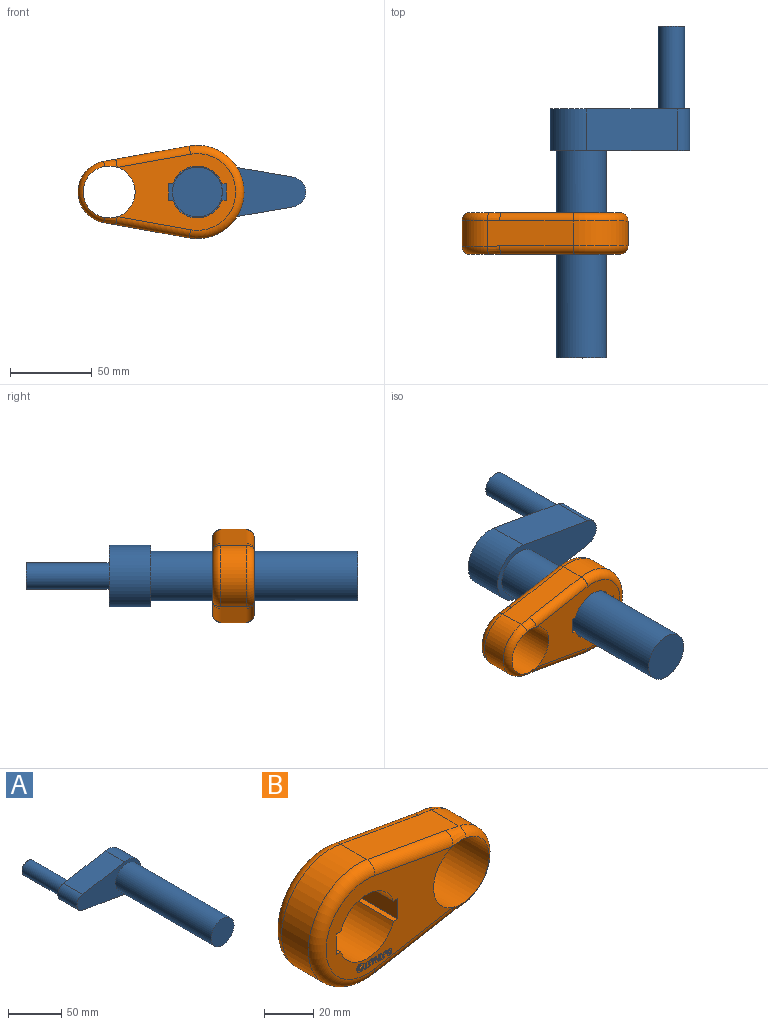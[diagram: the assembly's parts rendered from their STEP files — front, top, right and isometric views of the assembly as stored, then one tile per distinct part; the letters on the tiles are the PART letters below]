
ASSEMBLY  parts=2 mates=1
PART A: 10 faces, bbox 85.4x203.2x37.8 mm
  f0: cylinder r=15.24mm len=127mm, axis (0,1,0), area 12161mm2, adj f1,f6
  f1: plane 30.48x30.48mm, normal (0,-1,0), area 729.7mm2, adj f0
  f2: plane 55.6x25.4mm, normal (-0.17,0,0.99), area 1433.1mm2, adj f3,f5,f6,f7
  f3: cylinder r=9.2mm len=25.4mm, axis (0,1,0), area 654.5mm2, adj f2,f4,f6,f7
  f4: plane 55.6x25.4mm, normal (-0.17,0,-0.99), area 1433.1mm2, adj f3,f5,f6,f7
  f5: cylinder r=18.91mm len=37.83mm, axis (0,1,0), area 1672.9mm2, adj f2,f4,f6,f7
  f6: plane 85.36x37.83mm, normal (0,-1,0), area 1597.9mm2, adj f0,f2,f3,f4,f5
  f7: plane 85.36x37.83mm, normal (0,1,0), area 2123.6mm2, adj f2,f3,f4,f5,f8
  f8: cylinder r=8.06mm len=50.8mm, axis (0,-1,0), area 2571.5mm2, adj f7,f9
  f9: plane 16.11x16.11mm, normal (0,1,0), area 203.9mm2, adj f8
PART B: 155 faces, bbox 105.5x27.1x61.9 mm
  f0: plane 72.51x46.99mm, normal (0,-1,0), area 1669.8mm2, adj f2,f3,f4,f5,f6,f7,f8,f9
  f1: cylinder r=28.57mm len=57.15mm, axis (0,1,0), area 1522.6mm2, adj f11,f12,f15,f23
  f2: cylinder r=15.88mm len=30.08mm, axis (0,1,0), area 1004.1mm2, adj f0,f3,f9,f10
  f3: plane 25.4x2.55mm, normal (0,0,-1), area 64.9mm2, adj f0,f2,f4,f10
  f4: plane 25.4x10.16mm, normal (-1,0,0), area 258.1mm2, adj f0,f3,f5,f10
  f5: plane 25.4x2.55mm, normal (0,0,1), area 64.9mm2, adj f0,f4,f6,f10
  f6: cylinder r=15.88mm len=30.08mm, axis (0,1,0), area 1004.1mm2, adj f0,f5,f7,f10
  f7: plane 25.4x2.55mm, normal (0,0,1), area 64.9mm2, adj f0,f6,f8,f10
  f8: plane 25.4x10.16mm, normal (1,0,0), area 258.1mm2, adj f0,f7,f9,f10
  f9: plane 25.4x2.55mm, normal (0,0,-1), area 64.9mm2, adj f0,f2,f8,f10
  f10: plane 72.51x46.99mm, normal (0,1,0), area 1702mm2, adj f2,f3,f4,f5,f6,f7,f8,f9
  f11: plane 52.3x15.98mm, normal (0.18,0,0.98), area 812.6mm2, adj f1,f14,f16,f18,f21,f22
  f12: plane 52.3x15.98mm, normal (0.18,0,-0.98), area 812.6mm2, adj f1,f14,f17,f19,f25,f26
  f13: cylinder r=15.88mm len=31.75mm, axis (0,1,0), area 2533.5mm2, adj f0,f10,f18,f19,f20,f22,f24,f26
  f14: cylinder r=19.05mm len=37.5mm, axis (0,1,0), area 848.4mm2, adj f11,f12,f20,f24
  f15: torus R=23.49mm, axis (0,-1,0), area 745.7mm2, adj f1,f10,f16,f17
  f16: cylinder r=5.08mm len=45.77mm, axis (-0.98,0,0.18), area 363.8mm2, adj f10,f11,f15,f18
  f17: cylinder r=5.08mm len=45.77mm, axis (0.98,0,0.18), area 363.8mm2, adj f10,f12,f15,f19
  f18: bspline ~10.56x6.04mm, area 50.3mm2, adj f11,f13,f16,f20
  f19: bspline ~10.56x6.04mm, area 50.3mm2, adj f12,f13,f17,f20
  f20: torus R=13.97mm, axis (0,1,0), area 301.3mm2, adj f13,f14,f18,f19
  f21: cylinder r=5.08mm len=45.77mm, axis (0.98,0,-0.18), area 363.8mm2, adj f0,f11,f22,f23
  f22: bspline ~10.23x5.84mm, area 50.4mm2, adj f11,f13,f21,f24
  f23: torus R=23.49mm, axis (0,-1,0), area 745.7mm2, adj f0,f1,f21,f25
  f24: torus R=13.97mm, axis (0,-1,0), area 301.3mm2, adj f13,f14,f22,f26
  f25: cylinder r=5.08mm len=45.77mm, axis (-0.98,0,-0.18), area 363.8mm2, adj f0,f12,f23,f26
  f26: bspline ~10.23x5.84mm, area 50.4mm2, adj f12,f13,f24,f25
  f27: plane 0.64x0.25mm, normal (-1,0,0), area 0.2mm2, adj f0,f28,f45,f46
  f28: plane 0.68x0.25mm, normal (0,0,-1), area 0.2mm2, adj f0,f27,f29,f46
  f29: plane 0.75x0.25mm, normal (-1,0,0), area 0.2mm2, adj f0,f28,f30,f46
  f30: extruded ~0.49x0.25mm, area 0.1mm2, adj f0,f29,f31,f46
  f31: extruded ~0.7x0.31mm, area 0.2mm2, adj f0,f30,f32,f46
  f32: extruded ~0.9x0.25mm, area 0.2mm2, adj f0,f31,f33,f46
  f33: extruded ~0.89x0.3mm, area 0.2mm2, adj f0,f32,f34,f46
  f34: extruded ~0.79x0.33mm, area 0.2mm2, adj f0,f33,f35,f46
  f35: extruded ~0.82x0.25mm, area 0.2mm2, adj f0,f34,f36,f46
  f36: plane 0.61x0.25mm, normal (0.92,0,-0.38), area 0.2mm2, adj f0,f35,f37,f46
  f37: extruded ~1.07x0.25mm, area 0.3mm2, adj f0,f36,f38,f46
  f38: extruded ~1.38x0.49mm, area 0.4mm2, adj f0,f37,f39,f46
  f39: extruded ~1.36x0.5mm, area 0.4mm2, adj f0,f38,f40,f46
  f40: extruded ~1.38x0.43mm, area 0.4mm2, adj f0,f39,f41,f46
  f41: extruded ~1.24x0.48mm, area 0.3mm2, adj f0,f40,f42,f46
  f42: extruded ~0.63x0.25mm, area 0.2mm2, adj f0,f41,f43,f46
  f43: extruded ~0.65x0.25mm, area 0.2mm2, adj f0,f42,f44,f46
  f44: plane 1.87x0.25mm, normal (1,0,0), area 0.5mm2, adj f0,f43,f45,f46
  f45: plane 1.43x0.25mm, normal (0,0,1), area 0.4mm2, adj f0,f27,f44,f46
  f46: plane 3.7x2.95mm, normal (0,-1,0), area 6.3mm2, adj f27,f28,f29,f30,f31,f32,f33,f34
  f47: plane 0.58x0.25mm, normal (0,0,-1), area 0.1mm2, adj f0,f48,f63,f64
  f48: plane 2.75x0.25mm, normal (1,0,0), area 0.7mm2, adj f0,f47,f49,f64
  f49: plane 0.75x0.25mm, normal (0,0,1), area 0.2mm2, adj f0,f48,f50,f64
  f50: plane 1.3x0.25mm, normal (-1,0,0), area 0.3mm2, adj f0,f49,f51,f64
  f51: extruded ~0.7x0.25mm, area 0.2mm2, adj f0,f50,f52,f64
  f52: extruded ~0.46x0.25mm, area 0.1mm2, adj f0,f51,f53,f64
  f53: extruded ~0.34x0.25mm, area 0.1mm2, adj f0,f52,f54,f64
  f54: extruded ~0.45x0.25mm, area 0.1mm2, adj f0,f53,f55,f64
  f55: plane 1.61x0.25mm, normal (1,0,0), area 0.4mm2, adj f0,f54,f56,f64
  f56: plane 0.75x0.25mm, normal (0,0,1), area 0.2mm2, adj f0,f55,f57,f64
  f57: plane 1.79x0.25mm, normal (-1,0,0), area 0.5mm2, adj f0,f56,f58,f64
  f58: extruded ~0.75x0.25mm, area 0.2mm2, adj f0,f57,f59,f64
  f59: extruded ~0.73x0.26mm, area 0.2mm2, adj f0,f58,f60,f64
  f60: extruded ~0.5x0.25mm, area 0.1mm2, adj f0,f59,f61,f64
  f61: extruded ~0.34x0.3mm, area 0.1mm2, adj f0,f60,f62,f64
  f62: plane 0.25x0.04mm, normal (0,0,-1), area 0mm2, adj f0,f61,f63,f64
  f63: plane 0.35x0.25mm, normal (-0.96,0,-0.28), area 0.1mm2, adj f0,f47,f62,f64
  f64: plane 2.8x2.54mm, normal (0,-1,0), area 4.6mm2, adj f47,f48,f49,f50,f51,f52,f53,f54
  f65: plane 1.38x0.25mm, normal (1,0,0), area 0.4mm2, adj f0,f66,f92,f93
  f66: extruded ~0.63x0.25mm, area 0.2mm2, adj f0,f65,f67,f93
  f67: extruded ~0.41x0.25mm, area 0.1mm2, adj f0,f66,f68,f93
  f68: extruded ~0.31x0.25mm, area 0.1mm2, adj f0,f67,f69,f93
  f69: extruded ~0.45x0.25mm, area 0.1mm2, adj f0,f68,f70,f93
  f70: plane 1.61x0.25mm, normal (-1,0,0), area 0.4mm2, adj f0,f69,f71,f93
  f71: plane 0.75x0.25mm, normal (0,0,-1), area 0.2mm2, adj f0,f70,f72,f93
  f72: plane 1.79x0.25mm, normal (1,0,0), area 0.5mm2, adj f0,f71,f73,f93
  f73: extruded ~0.77x0.25mm, area 0.2mm2, adj f0,f72,f74,f93
  f74: extruded ~0.71x0.25mm, area 0.2mm2, adj f0,f73,f75,f93
  f75: extruded ~0.49x0.25mm, area 0.1mm2, adj f0,f74,f76,f93
  f76: extruded ~0.33x0.3mm, area 0.1mm2, adj f0,f75,f77,f93
  f77: plane 0.25x0.07mm, normal (0,0,1), area 0mm2, adj f0,f76,f78,f93
  f78: extruded ~0.84x0.4mm, area 0.2mm2, adj f0,f77,f79,f93
  f79: extruded ~0.48x0.25mm, area 0.1mm2, adj f0,f78,f80,f93
  f80: extruded ~0.32x0.3mm, area 0.1mm2, adj f0,f79,f81,f93
  f81: plane 0.25x0.04mm, normal (0,0,1), area 0mm2, adj f0,f80,f82,f93
  f82: plane 0.35x0.25mm, normal (0.96,0,0.28), area 0.1mm2, adj f0,f81,f83,f93
  f83: plane 0.57x0.25mm, normal (0,0,1), area 0.1mm2, adj f0,f82,f84,f93
  f84: plane 2.75x0.25mm, normal (-1,0,0), area 0.7mm2, adj f0,f83,f85,f93
  f85: plane 0.75x0.25mm, normal (0,0,-1), area 0.2mm2, adj f0,f84,f86,f93
  f86: plane 1.3x0.25mm, normal (1,0,0), area 0.3mm2, adj f0,f85,f87,f93
  f87: extruded ~0.7x0.25mm, area 0.2mm2, adj f0,f86,f88,f93
  f88: extruded ~0.42x0.25mm, area 0.1mm2, adj f0,f87,f89,f93
  f89: extruded ~0.31x0.25mm, area 0.1mm2, adj f0,f88,f90,f93
  f90: extruded ~0.45x0.25mm, area 0.1mm2, adj f0,f89,f91,f93
  f91: plane 1.61x0.25mm, normal (-1,0,0), area 0.4mm2, adj f0,f90,f92,f93
  f92: plane 0.75x0.25mm, normal (0,0,-1), area 0.2mm2, adj f0,f65,f91,f93
  f93: plane 4.18x2.8mm, normal (0,-1,0), area 7.2mm2, adj f65,f66,f67,f68,f69,f70,f71,f72
  f94: plane 0.52x0.25mm, normal (0,0,-1), area 0.1mm2, adj f0,f95,f118,f119
  f95: plane 1.83x0.25mm, normal (1,0,0), area 0.5mm2, adj f0,f94,f96,f119
  f96: extruded ~0.73x0.3mm, area 0.2mm2, adj f0,f95,f97,f119
  f97: extruded ~0.85x0.25mm, area 0.2mm2, adj f0,f96,f98,f119
  f98: extruded ~1.05x0.25mm, area 0.3mm2, adj f0,f97,f99,f119
  f99: plane 0.51x0.25mm, normal (-0.9,0,-0.44), area 0.1mm2, adj f0,f98,f100,f119
  f100: extruded ~0.78x0.25mm, area 0.2mm2, adj f0,f99,f101,f119
  f101: extruded ~0.43x0.42mm, area 0.2mm2, adj f0,f100,f102,f119
  f102: plane 0.25x0.12mm, normal (-1,0,0), area 0mm2, adj f0,f101,f103,f119
  f103: plane 0.48x0.25mm, normal (-0.03,0,1), area 0.1mm2, adj f0,f102,f104,f119
  f104: extruded ~0.92x0.25mm, area 0.2mm2, adj f0,f103,f105,f119
  f105: extruded ~0.65x0.31mm, area 0.2mm2, adj f0,f104,f106,f119
  f106: extruded ~0.65x0.25mm, area 0.2mm2, adj f0,f105,f107,f119
  f107: extruded ~0.62x0.25mm, area 0.2mm2, adj f0,f106,f108,f119
  f108: extruded ~0.52x0.25mm, area 0.1mm2, adj f0,f107,f109,f119
  f109: extruded ~0.39x0.33mm, area 0.1mm2, adj f0,f108,f110,f119
  f110: plane 0.25x0.02mm, normal (0,0,-1), area 0mm2, adj f0,f109,f118,f119
  f111: plane 0.25x0.23mm, normal (-1,0,0), area 0.1mm2, adj f112,f117,f119,f120
  f112: extruded ~0.4x0.25mm, area 0.1mm2, adj f111,f113,f119,f120
  f113: extruded ~0.42x0.25mm, area 0.1mm2, adj f112,f114,f119,f120
  f114: extruded ~0.36x0.32mm, area 0.1mm2, adj f113,f115,f119,f120
  f115: extruded ~0.33x0.25mm, area 0.1mm2, adj f114,f116,f119,f120
  f116: extruded ~0.49x0.25mm, area 0.1mm2, adj f115,f117,f119,f120
  f117: plane 0.29x0.25mm, normal (0.04,0,-1), area 0.1mm2, adj f111,f116,f119,f120
  f118: plane 0.37x0.25mm, normal (-0.93,0,-0.36), area 0.1mm2, adj f0,f94,f110,f119
  f119: plane 2.86x2.45mm, normal (0,-1,0), area 4.6mm2, adj f94,f95,f96,f97,f98,f99,f100,f101
  f120: plane 0.94x0.78mm, normal (0,-1,0), area 0.6mm2, adj f111,f112,f113,f114,f115,f116,f117
  f121: extruded ~0.47x0.25mm, area 0.1mm2, adj f0,f122,f133,f134
  f122: extruded ~0.37x0.35mm, area 0.1mm2, adj f0,f121,f123,f134
  f123: plane 0.25x0.04mm, normal (0,0,1), area 0mm2, adj f0,f122,f124,f134
  f124: plane 0.46x0.25mm, normal (0.97,0,0.23), area 0.1mm2, adj f0,f123,f125,f134
  f125: plane 0.57x0.25mm, normal (0,0,1), area 0.1mm2, adj f0,f124,f126,f134
  f126: plane 2.75x0.25mm, normal (-1,0,0), area 0.7mm2, adj f0,f125,f127,f134
  f127: plane 0.75x0.25mm, normal (0,0,-1), area 0.2mm2, adj f0,f126,f128,f134
  f128: plane 1.4x0.25mm, normal (1,0,0), area 0.4mm2, adj f0,f127,f129,f134
  f129: extruded ~0.52x0.25mm, area 0.1mm2, adj f0,f128,f130,f134
  f130: extruded ~0.56x0.25mm, area 0.2mm2, adj f0,f129,f131,f134
  f131: extruded ~0.25x0.22mm, area 0.1mm2, adj f0,f130,f132,f134
  f132: plane 0.7x0.25mm, normal (1,0,-0.08), area 0.2mm2, adj f0,f131,f133,f134
  f133: extruded ~0.25x0.25mm, area 0.1mm2, adj f0,f121,f132,f134
  f134: plane 2.8x1.79mm, normal (0,-1,0), area 2.7mm2, adj f121,f122,f123,f124,f125,f126,f127,f128
  f135: extruded ~0.61x0.25mm, area 0.2mm2, adj f136,f152,f153,f154
  f136: extruded ~0.43x0.25mm, area 0.1mm2, adj f135,f137,f153,f154
  f137: extruded ~0.44x0.25mm, area 0.1mm2, adj f136,f138,f153,f154
  f138: extruded ~0.61x0.25mm, area 0.2mm2, adj f137,f139,f153,f154
  f139: extruded ~0.62x0.25mm, area 0.2mm2, adj f138,f140,f153,f154
  f140: extruded ~0.43x0.25mm, area 0.1mm2, adj f139,f141,f153,f154
  f141: extruded ~0.44x0.25mm, area 0.1mm2, adj f140,f152,f153,f154
  f142: extruded ~0.76x0.25mm, area 0.2mm2, adj f0,f143,f151,f153
  f143: extruded ~0.49x0.47mm, area 0.2mm2, adj f0,f142,f144,f153
  f144: extruded ~0.7x0.25mm, area 0.2mm2, adj f0,f143,f145,f153
  f145: extruded ~0.99x0.37mm, area 0.3mm2, adj f0,f144,f146,f153
  f146: extruded ~1.05x0.35mm, area 0.3mm2, adj f0,f145,f147,f153
  f147: extruded ~0.76x0.25mm, area 0.2mm2, adj f0,f146,f148,f153
  f148: extruded ~0.5x0.47mm, area 0.2mm2, adj f0,f147,f149,f153
  f149: extruded ~0.7x0.25mm, area 0.2mm2, adj f0,f148,f150,f153
  f150: extruded ~0.99x0.38mm, area 0.3mm2, adj f0,f149,f151,f153
  f151: extruded ~1.05x0.35mm, area 0.3mm2, adj f0,f142,f150,f153
  f152: extruded ~0.62x0.25mm, area 0.2mm2, adj f135,f141,f153,f154
  f153: plane 2.85x2.67mm, normal (0,-1,0), area 4.6mm2, adj f135,f136,f137,f138,f139,f140,f141,f142
  f154: plane 1.65x1.14mm, normal (0,-1,0), area 1.6mm2, adj f135,f136,f137,f138,f139,f140,f141,f152
PLACE A rot(axis=(0,-1,0),180deg) t=(12.76,154.42,-40.67)mm
PLACE B rot(axis=(0,0,-1),180deg) t=(12.76,65.52,-40.67)mm
MATE pin_slot A.f0 <-> B.f1  axis (0,1,0) through (12.76,65.52,-40.67)mm
